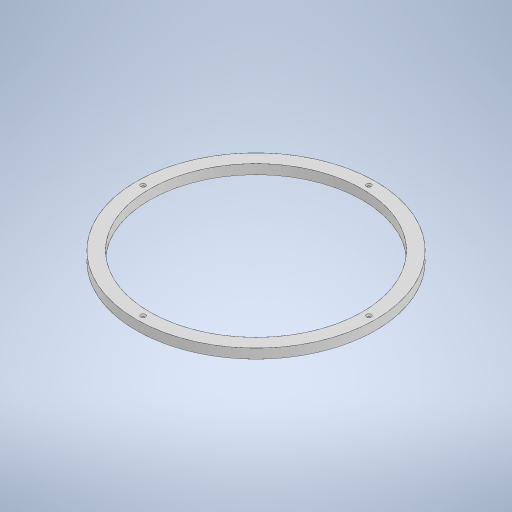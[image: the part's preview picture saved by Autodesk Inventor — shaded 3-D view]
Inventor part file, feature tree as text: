
AUTODESK INVENTOR PART (.ipt)
format: ipt  version: 2023 (Build 270158000, 158)  size: 256,512 bytes
history: native  units: in
note: dims shown in document units (in); Inventor stores cm internally (conversion verified against a paired STEP export)
features: sketch x2, extrude x1, hole x1, pattern_circular x1
ambient origin geometry x8: Origin, YZ Plane, XZ Plane, XY Plane, X Axis, Y Axis, Z Axis, Center Point
bodies: Solid1 (feature_tree)
feature tree (5):
  extrude  "Extrusion1"  Depth=8.7598in
  hole  "Hole1"  [1 undecoded]
  pattern_circular  "Circular Pattern1"  Count=4 Angle=360.0deg
  sketch  "Sketch1"  dims[d0=9.8425in d1=8.7598in]
  sketch  "Sketch2"  dims[d2=0.3937in d3=0.0in d4=9.3012in d6=0.0984in d7=0.2362in d8=0.1969in d9=0.0787in d10=90.0deg d11=0.315in d12=0.8108in d13=1.5748in d14=360.0deg]
note: 1 required parameter value undecoded (feature->parameter linkage not recoverable at this tier; creation-order binding heuristic only, values carry confidence <= 0.55)
